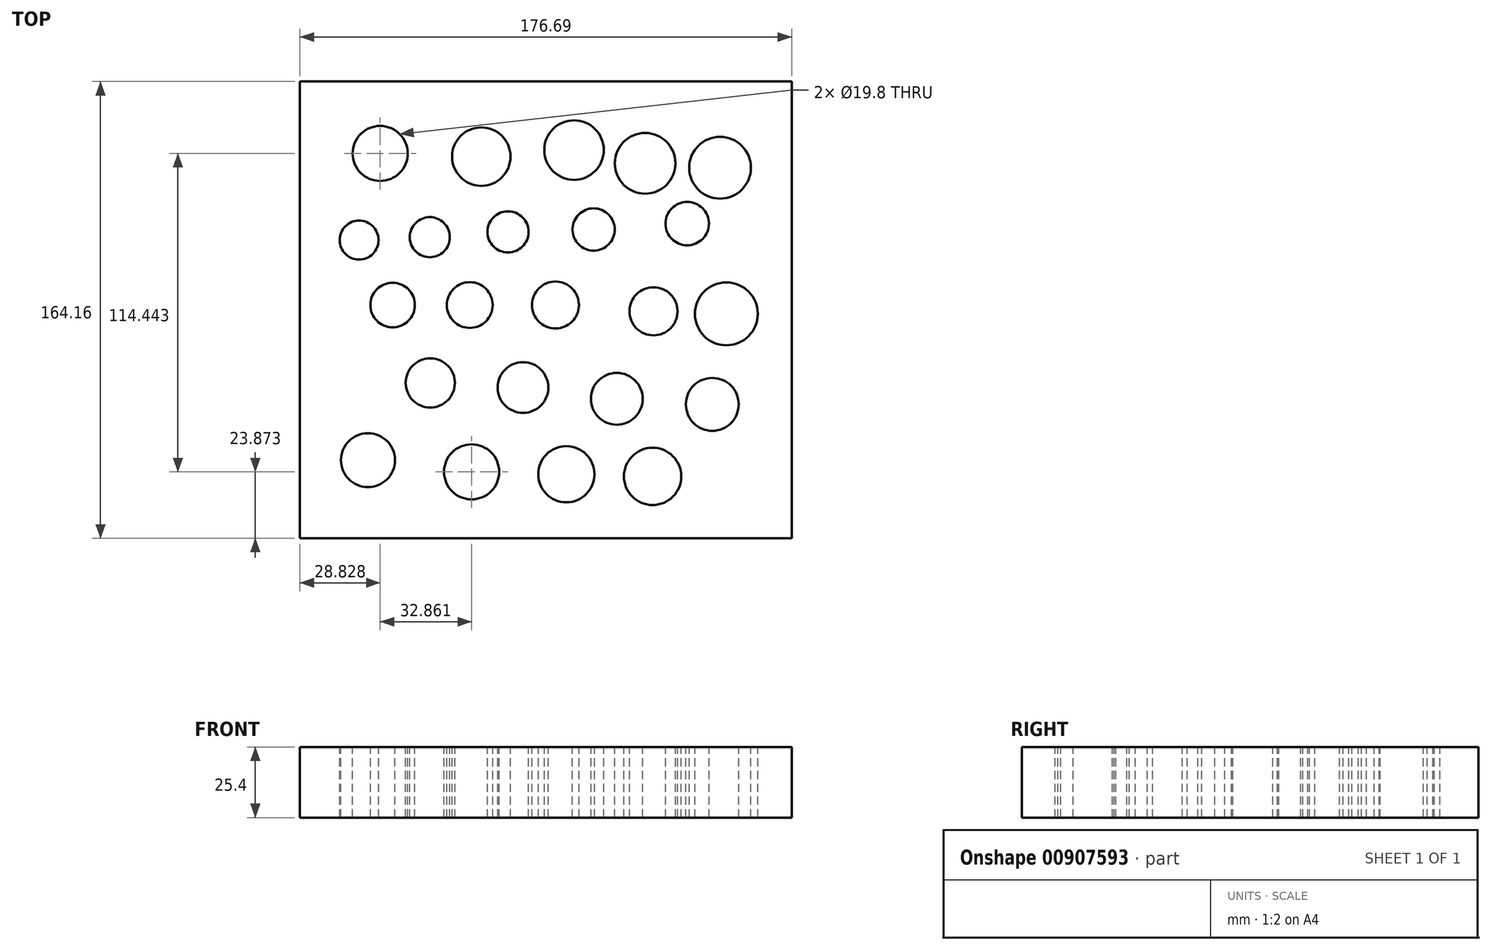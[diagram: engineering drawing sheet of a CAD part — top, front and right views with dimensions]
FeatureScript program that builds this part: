
annotation { "Feature Type Name" : "Feature", "Feature Type Description" : "" }
export const myFeature = defineFeature(function(context is Context, id is Id, definition is map)
    precondition{}
    {
        {
            var Q0;
            Q0=qCreatedBy(makeId("Top.planeOp"),FACE);
            var sketch = newSketch(context, id + "F0", { "sketchPlane" : qUnion([Q0])});
            skCircle(sketch, "E0", {"center": v(-64.47, 30.3) * mm, "radius": 7 * mm});
            skSolve(sketch);
        }
        {
            var Q0;
            Q0=qCreatedBy(makeId("Top.planeOp"),FACE);
            var sketch = newSketch(context, id + "F1", { "sketchPlane" : qUnion([Q0])});
            skCircle(sketch, "E1", {"center": v(-39.06, 31.35) * mm, "radius": 7.2 * mm});
            skCircle(sketch, "E2", {"center": v(-39.06, 31.35) * mm, "radius": 13.34 * mm});
            skSolve(sketch);
        }
        {
            var Q0;
            Q0=qCreatedBy(makeId("Top.planeOp"),FACE);
            var sketch = newSketch(context, id + "F2", { "sketchPlane" : qUnion([Q0])});
            skCircle(sketch, "E3", {"center": v(-10.97, 33.25) * mm, "radius": 7.4 * mm});
            skSolve(sketch);
        }
        {
            var Q0;
            Q0=qCreatedBy(makeId("Top.planeOp"),FACE);
            var sketch = newSketch(context, id + "F3", { "sketchPlane" : qUnion([Q0])});
            skCircle(sketch, "E4", {"center": v(19.81, 34.1) * mm, "radius": 7.6 * mm});
            skCircle(sketch, "E5", {"center": v(19.81, 34.1) * mm, "radius": 16.16 * mm});
            skSolve(sketch);
        }
        {
            var Q0;
            Q0=qCreatedBy(makeId("Top.planeOp"),FACE);
            var sketch = newSketch(context, id + "F4", { "sketchPlane" : qUnion([Q0])});
            skCircle(sketch, "E6", {"center": v(53.45, 36.22) * mm, "radius": 7.8 * mm});
            skCircle(sketch, "E7", {"center": v(53.45, 36.22) * mm, "radius": 17.23 * mm});
            skSolve(sketch);
        }
        {
            var Q0;
            Q0=qCreatedBy(makeId("Top.planeOp"),FACE);
            var sketch = newSketch(context, id + "F5", { "sketchPlane" : qUnion([Q0])});
            skCircle(sketch, "E8", {"center": v(-52.42, 6.95) * mm, "radius": 8 * mm});
            skCircle(sketch, "E9", {"center": v(-52.42, 6.95) * mm, "radius": 14.7 * mm});
            skCircle(sketch, "E10", {"center": v(-24.7, 6.95) * mm, "radius": 8.22 * mm});
            skCircle(sketch, "E11", {"center": v(-24.7, 6.95) * mm, "radius": 14.91 * mm});
            skCircle(sketch, "E12", {"center": v(6.09, 6.95) * mm, "radius": 8.45 * mm});
            skCircle(sketch, "E13", {"center": v(6.09, 6.95) * mm, "radius": 17.16 * mm});
            skCircle(sketch, "E14", {"center": v(41.32, 4.7) * mm, "radius": 8.65 * mm});
            skCircle(sketch, "E15", {"center": v(41.32, 4.7) * mm, "radius": 20.93 * mm});
            skSolve(sketch);
        }
        {
            var Q0;
            Q0=qCreatedBy(makeId("Top.planeOp"),FACE);
            var sketch = newSketch(context, id + "F6", { "sketchPlane" : qUnion([Q0])});
            skCircle(sketch, "E16", {"center": v(-38.88, -21.03) * mm, "radius": 8.85 * mm});
            skCircle(sketch, "E17", {"center": v(-38.88, -21.03) * mm, "radius": 16.78 * mm});
            skCircle(sketch, "E18", {"center": v(-5.56, -22.7) * mm, "radius": 9.1 * mm});
            skCircle(sketch, "E19", {"center": v(-5.56, -22.7) * mm, "radius": 17.22 * mm});
            skCircle(sketch, "E20", {"center": v(28.14, -26.75) * mm, "radius": 9.3 * mm});
            skCircle(sketch, "E21", {"center": v(28.14, -26.75) * mm, "radius": 17.82 * mm});
            skCircle(sketch, "E22", {"center": v(62.46, -28.75) * mm, "radius": 9.5 * mm});
            skCircle(sketch, "E23", {"center": v(62.46, -28.75) * mm, "radius": 19.12 * mm});
            skCircle(sketch, "E24", {"center": v(-61.27, -48.8) * mm, "radius": 9.7 * mm});
            skCircle(sketch, "E25", {"center": v(-61.27, -48.8) * mm, "radius": 18.92 * mm});
            skCircle(sketch, "E26", {"center": v(-24.03, -53) * mm, "radius": 9.9 * mm});
            skCircle(sketch, "E27", {"center": v(-24.03, -53) * mm, "radius": 19.02 * mm});
            skCircle(sketch, "E28", {"center": v(10, -53.86) * mm, "radius": 10.1 * mm});
            skCircle(sketch, "E29", {"center": v(10, -53.86) * mm, "radius": 15.87 * mm});
            skCircle(sketch, "E30", {"center": v(41, -54.64) * mm, "radius": 10.3 * mm});
            skCircle(sketch, "E31", {"center": v(41, -54.64) * mm, "radius": 15.98 * mm});
            skSolve(sketch);
        }
        {
            var Q0;
            Q0=qCreatedBy(makeId("Top.planeOp"),FACE);
            var sketch = newSketch(context, id + "F7", { "sketchPlane" : qUnion([Q0])});
            skCircle(sketch, "E32", {"center": v(-56.9, 61.44) * mm, "radius": 9.9 * mm});
            skCircle(sketch, "E33", {"center": v(-56.9, 61.44) * mm, "radius": 22.06 * mm});
            skSolve(sketch);
        }
        {
            var Q0;
            Q0=qCreatedBy(makeId("Top.planeOp"),FACE);
            var sketch = newSketch(context, id + "F8", { "sketchPlane" : qUnion([Q0])});
            skCircle(sketch, "E34", {"center": v(-20.55, 60.3) * mm, "radius": 10.5 * mm});
            skCircle(sketch, "E35", {"center": v(-20.55, 60.3) * mm, "radius": 14.75 * mm});
            skSolve(sketch);
        }
        {
            var Q0;
            Q0=qCreatedBy(makeId("Top.planeOp"),FACE);
            var sketch = newSketch(context, id + "F9", { "sketchPlane" : qUnion([Q0])});
            skCircle(sketch, "E36", {"center": v(12.78, 62.65) * mm, "radius": 10.7 * mm});
            skCircle(sketch, "E37", {"center": v(12.78, 62.65) * mm, "radius": 14.65 * mm});
            skSolve(sketch);
        }
        {
            var Q0;
            Q0=qCreatedBy(makeId("Top.planeOp"),FACE);
            var sketch = newSketch(context, id + "F10", { "sketchPlane" : qUnion([Q0])});
            skLineSegment(sketch, "E38.bottom", {"start": v(-85.72, 87.28) * mm, "end": v(90.97, 87.28) * mm});
            skLineSegment(sketch, "E38.top", {"start": v(-85.72, -76.88) * mm, "end": v(90.97, -76.88) * mm});
            skLineSegment(sketch, "E38.left", {"start": v(-85.72, 87.28) * mm, "end": v(-85.72, -76.88) * mm});
            skLineSegment(sketch, "E38.right", {"start": v(90.97, 87.28) * mm, "end": v(90.97, -76.88) * mm});
            skSolve(sketch);
        }
        {
            var Q0;
            Q0 = qSketchRegion(id + "F10", true);
            extrude(context, id + "F11", {"entities" : qUnion([Q0]), "oppositeDirection" : true, "depth" : 25.4 * mm, "offsetDistance" : 25.4 * mm});
        }
        {
            var Q0;
            Q0=makeQuery(id+"F7.imprint","IMPRINT",FACE,{"disambiguationData":[TD([[makeQuery(id+"F7.imprint","IMPRINT",EDGE,{"derivedFrom":sQuery(id+"F7.wireOp",EDGE,"E32")}),1.0]])]});
            extrude(context, id + "F12", {"entities" : qUnion([Q0]), "operationType" : NewBodyOperationType.REMOVE, "oppositeDirection" : true, "depth" : 25.4 * mm, "offsetDistance" : 25.4 * mm});
        }
        {
            var Q0;
            Q0=makeQuery(id+"F8.imprint","IMPRINT",FACE,{"disambiguationData":[TD([[makeQuery(id+"F8.imprint","IMPRINT",EDGE,{"derivedFrom":sQuery(id+"F8.wireOp",EDGE,"E34")}),1.0]])]});
            extrude(context, id + "F13", {"entities" : qUnion([Q0]), "operationType" : NewBodyOperationType.REMOVE, "oppositeDirection" : true, "depth" : 25.4 * mm, "offsetDistance" : 25.4 * mm});
        }
        {
            var Q0;
            Q0=makeQuery(id+"F9.imprint","IMPRINT",FACE,{"disambiguationData":[TD([[makeQuery(id+"F9.imprint","IMPRINT",EDGE,{"derivedFrom":sQuery(id+"F9.wireOp",EDGE,"E36")}),1.0]])]});
            extrude(context, id + "F14", {"entities" : qUnion([Q0]), "operationType" : NewBodyOperationType.REMOVE, "oppositeDirection" : true, "depth" : 25.4 * mm, "offsetDistance" : 25.4 * mm});
        }
        {
            var Q0;
            Q0=makeQuery(id+"F0.imprint","IMPRINT",FACE,{"disambiguationData":[TD([[makeQuery(id+"F0.imprint","IMPRINT",EDGE,{"derivedFrom":sQuery(id+"F0.wireOp",EDGE,"E0")}),1.0]])]});
            extrude(context, id + "F15", {"entities" : qUnion([Q0]), "operationType" : NewBodyOperationType.REMOVE, "oppositeDirection" : true, "depth" : 25.4 * mm, "offsetDistance" : 25.4 * mm});
        }
        {
            var Q0;
            Q0=makeQuery(id+"F1.imprint","IMPRINT",FACE,{"disambiguationData":[TD([[makeQuery(id+"F1.imprint","IMPRINT",EDGE,{"derivedFrom":sQuery(id+"F1.wireOp",EDGE,"E1")}),1.0]])]});
            extrude(context, id + "F16", {"entities" : qUnion([Q0]), "operationType" : NewBodyOperationType.REMOVE, "oppositeDirection" : true, "depth" : 25.4 * mm, "offsetDistance" : 25.4 * mm});
        }
        {
            var Q0;
            Q0=makeQuery(id+"F3.imprint","IMPRINT",FACE,{"disambiguationData":[TD([[makeQuery(id+"F3.imprint","IMPRINT",EDGE,{"derivedFrom":sQuery(id+"F3.wireOp",EDGE,"E4")}),1.0]])]});
            extrude(context, id + "F17", {"entities" : qUnion([Q0]), "operationType" : NewBodyOperationType.REMOVE, "oppositeDirection" : true, "depth" : 25.4 * mm, "offsetDistance" : 25.4 * mm});
        }
        {
            var Q0;
            Q0=makeQuery(id+"F2.imprint","IMPRINT",FACE,{"disambiguationData":[TD([[makeQuery(id+"F2.imprint","IMPRINT",EDGE,{"derivedFrom":sQuery(id+"F2.wireOp",EDGE,"E3")}),1.0]])]});
            extrude(context, id + "F18", {"entities" : qUnion([Q0]), "operationType" : NewBodyOperationType.REMOVE, "oppositeDirection" : true, "depth" : 25.4 * mm, "offsetDistance" : 25.4 * mm});
        }
        {
            var Q0;
            Q0=makeQuery(id+"F4.imprint","IMPRINT",FACE,{"disambiguationData":[TD([[makeQuery(id+"F4.imprint","IMPRINT",EDGE,{"derivedFrom":sQuery(id+"F4.wireOp",EDGE,"E6")}),1.0]])]});
            extrude(context, id + "F19", {"entities" : qUnion([Q0]), "operationType" : NewBodyOperationType.REMOVE, "oppositeDirection" : true, "depth" : 25.4 * mm, "offsetDistance" : 25.4 * mm});
        }
        {
            var Q0;
            Q0=makeQuery(id+"F5.imprint","IMPRINT",FACE,{"disambiguationData":[TD([[makeQuery(id+"F5.imprint","IMPRINT",EDGE,{"derivedFrom":sQuery(id+"F5.wireOp",EDGE,"E8")}),1.0]])]});
            var Q1;
            Q1=makeQuery(id+"F5.imprint","IMPRINT",FACE,{"disambiguationData":[TD([[makeQuery(id+"F5.imprint","IMPRINT",EDGE,{"derivedFrom":sQuery(id+"F5.wireOp",EDGE,"E10")}),1.0]])]});
            var Q2;
            Q2=makeQuery(id+"F5.imprint","IMPRINT",FACE,{"disambiguationData":[TD([[makeQuery(id+"F5.imprint","IMPRINT",EDGE,{"derivedFrom":sQuery(id+"F5.wireOp",EDGE,"E12")}),1.0]])]});
            var Q3;
            Q3=makeQuery(id+"F5.imprint","IMPRINT",FACE,{"disambiguationData":[TD([[makeQuery(id+"F5.imprint","IMPRINT",EDGE,{"derivedFrom":sQuery(id+"F5.wireOp",EDGE,"E14")}),1.0]])]});
            extrude(context, id + "F20", {"entities" : qUnion([Q0, Q1, Q2, Q3]), "operationType" : NewBodyOperationType.REMOVE, "oppositeDirection" : true, "depth" : 25.4 * mm, "offsetDistance" : 25.4 * mm});
        }
        {
            var Q0;
            Q0=makeQuery(id+"F6.imprint","IMPRINT",FACE,{"disambiguationData":[TD([[makeQuery(id+"F6.imprint","IMPRINT",EDGE,{"derivedFrom":sQuery(id+"F6.wireOp",EDGE,"E16")}),1.0]])]});
            var Q1;
            Q1=makeQuery(id+"F6.imprint","IMPRINT",FACE,{"disambiguationData":[TD([[makeQuery(id+"F6.imprint","IMPRINT",EDGE,{"derivedFrom":sQuery(id+"F6.wireOp",EDGE,"E18")}),1.0]])]});
            var Q2;
            Q2=makeQuery(id+"F6.imprint","IMPRINT",FACE,{"disambiguationData":[TD([[makeQuery(id+"F6.imprint","IMPRINT",EDGE,{"derivedFrom":sQuery(id+"F6.wireOp",EDGE,"E20")}),1.0]])]});
            var Q3;
            Q3=makeQuery(id+"F6.imprint","IMPRINT",FACE,{"disambiguationData":[TD([[makeQuery(id+"F6.imprint","IMPRINT",EDGE,{"derivedFrom":sQuery(id+"F6.wireOp",EDGE,"E22")}),1.0]])]});
            var Q4;
            Q4=makeQuery(id+"F6.imprint","IMPRINT",FACE,{"disambiguationData":[TD([[makeQuery(id+"F6.imprint","IMPRINT",EDGE,{"derivedFrom":sQuery(id+"F6.wireOp",EDGE,"E24")}),1.0]])]});
            var Q5;
            Q5=makeQuery(id+"F6.imprint","IMPRINT",FACE,{"disambiguationData":[TD([[makeQuery(id+"F6.imprint","IMPRINT",EDGE,{"derivedFrom":sQuery(id+"F6.wireOp",EDGE,"E26")}),1.0]])]});
            var Q6;
            Q6=makeQuery(id+"F6.imprint","IMPRINT",FACE,{"disambiguationData":[TD([[makeQuery(id+"F6.imprint","IMPRINT",EDGE,{"derivedFrom":sQuery(id+"F6.wireOp",EDGE,"E28")}),1.0]])]});
            var Q7;
            Q7=makeQuery(id+"F6.imprint","IMPRINT",FACE,{"disambiguationData":[TD([[makeQuery(id+"F6.imprint","IMPRINT",EDGE,{"derivedFrom":sQuery(id+"F6.wireOp",EDGE,"E30")}),1.0]])]});
            extrude(context, id + "F21", {"entities" : qUnion([Q0, Q1, Q2, Q3, Q4, Q5, Q6, Q7]), "operationType" : NewBodyOperationType.REMOVE, "oppositeDirection" : true, "depth" : 25.4 * mm, "offsetDistance" : 25.4 * mm});
        }
        {
            var Q0;
            Q0=makeQuery(id+"F11.opExtrude","CAP_FACE",FACE,{"disambiguationData":[OSD([sQuery(id+"F10.wireOp",EDGE,"E38.bottom"),sQuery(id+"F10.wireOp",EDGE,"E38.top"),sQuery(id+"F10.wireOp",EDGE,"E38.left"),sQuery(id+"F10.wireOp",EDGE,"E38.right")])],"isStart":true});
            var sketch = newSketch(context, id + "F22", { "sketchPlane" : qUnion([Q0])});
            skCircle(sketch, "E39", {"center": v(38.32, 57.88) * mm, "radius": 10.9 * mm});
            skSolve(sketch);
        }
        {
            var Q0;
            Q0=makeQuery(id+"F22.imprint","IMPRINT",FACE,{"disambiguationData":[TD([[makeQuery(id+"F22.imprint","IMPRINT",EDGE,{"derivedFrom":sQuery(id+"F22.wireOp",EDGE,"E39")}),1.0]])]});
            extrude(context, id + "F23", {"entities" : qUnion([Q0]), "operationType" : NewBodyOperationType.REMOVE, "oppositeDirection" : true, "depth" : 25.4 * mm, "offsetDistance" : 25.4 * mm});
        }
        {
            var Q0;
            Q0=makeQuery(id+"F11.opExtrude","CAP_FACE",FACE,{"disambiguationData":[OSD([sQuery(id+"F10.wireOp",EDGE,"E38.bottom"),sQuery(id+"F10.wireOp",EDGE,"E38.top"),sQuery(id+"F10.wireOp",EDGE,"E38.left"),sQuery(id+"F10.wireOp",EDGE,"E38.right")])],"isStart":true});
            var sketch = newSketch(context, id + "F24", { "sketchPlane" : qUnion([Q0])});
            skCircle(sketch, "E40", {"center": v(65.25, 56.3) * mm, "radius": 11.1 * mm});
            skSolve(sketch);
        }
        {
            var Q0;
            Q0=makeQuery(id+"F24.imprint","IMPRINT",FACE,{"disambiguationData":[TD([[makeQuery(id+"F24.imprint","IMPRINT",EDGE,{"derivedFrom":sQuery(id+"F24.wireOp",EDGE,"E40")}),1.0]])]});
            extrude(context, id + "F25", {"entities" : qUnion([Q0]), "operationType" : NewBodyOperationType.REMOVE, "oppositeDirection" : true, "depth" : 25.4 * mm, "offsetDistance" : 25.4 * mm});
        }
        {
            var Q0;
            Q0=makeQuery(id+"F11.opExtrude","CAP_FACE",FACE,{"disambiguationData":[OSD([sQuery(id+"F10.wireOp",EDGE,"E38.bottom"),sQuery(id+"F10.wireOp",EDGE,"E38.top"),sQuery(id+"F10.wireOp",EDGE,"E38.left"),sQuery(id+"F10.wireOp",EDGE,"E38.right")])],"isStart":true});
            var sketch = newSketch(context, id + "F26", { "sketchPlane" : qUnion([Q0])});
            skCircle(sketch, "E41", {"center": v(67.5, 3.79) * mm, "radius": 11.3 * mm});
            skSolve(sketch);
        }
        {
            var Q0;
            Q0 = qSketchRegion(id + "F26", true);
            extrude(context, id + "F27", {"entities" : qUnion([Q0]), "operationType" : NewBodyOperationType.REMOVE, "oppositeDirection" : true, "depth" : 25.4 * mm, "offsetDistance" : 25.4 * mm});
        }
    });
